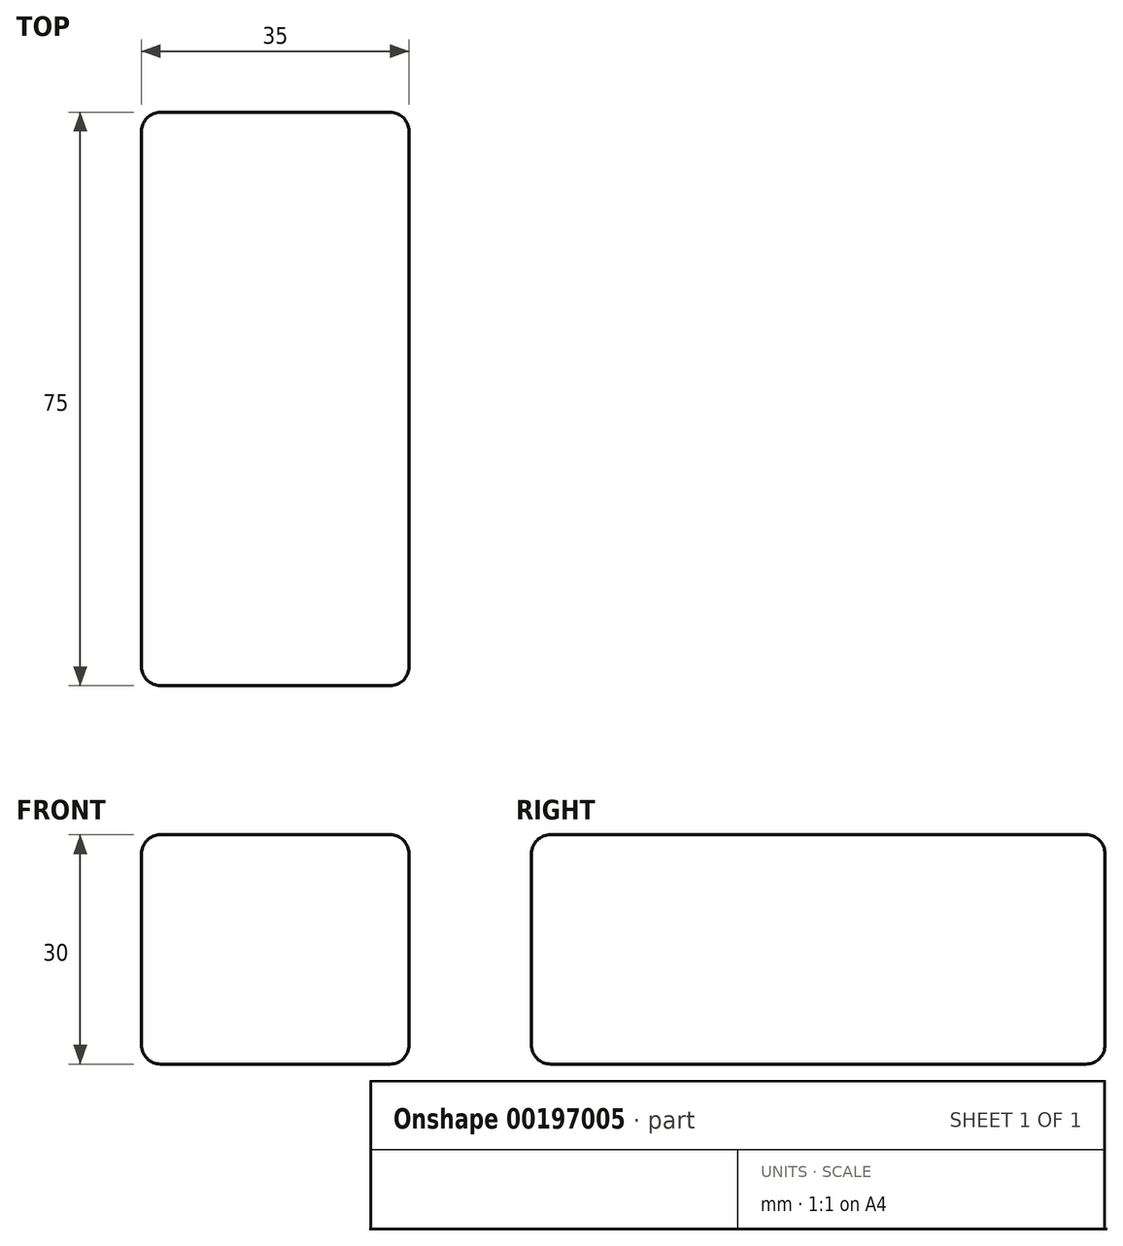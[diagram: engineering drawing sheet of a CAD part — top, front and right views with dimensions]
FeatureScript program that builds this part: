
annotation { "Feature Type Name" : "Feature", "Feature Type Description" : "" }
export const myFeature = defineFeature(function(context is Context, id is Id, definition is map)
    precondition{}
    {
        {
            var Q0;
            Q0=qCreatedBy(makeId("Top.planeOp"),FACE);
            var sketch = newSketch(context, id + "F0", { "sketchPlane" : qUnion([Q0])});
            skLineSegment(sketch, "E0.bottom", {"start": v(17.5, 37.5) * mm, "end": v(-17.5, 37.5) * mm});
            skLineSegment(sketch, "E0.top", {"start": v(17.5, -37.5) * mm, "end": v(-17.5, -37.5) * mm});
            skLineSegment(sketch, "E0.left", {"start": v(17.5, 37.5) * mm, "end": v(17.5, -37.5) * mm});
            skLineSegment(sketch, "E0.right", {"start": v(-17.5, 37.5) * mm, "end": v(-17.5, -37.5) * mm});
            skPoint(sketch, "E0.middle", {"position": v(0, 0) * mm});
            skSolve(sketch);
        }
        {
            var Q0;
            Q0 = qSketchRegion(id + "F0", true);
            extrude(context, id + "F1", {"entities" : qUnion([Q0]), "depth" : 30 * mm});
        }
        {
            var Q0;
            Q0=makeQuery(id+"F1.opExtrude","CAP_EDGE",EDGE,{"disambiguationData":[OSD([sQuery(id+"F0.wireOp",EDGE,"E0.bottom")])],"isStart":false});
            var Q1;
            Q1=makeQuery(id+"F1.opExtrude","CAP_EDGE",EDGE,{"disambiguationData":[OSD([sQuery(id+"F0.wireOp",EDGE,"E0.right")])],"isStart":false});
            var Q2;
            Q2=makeQuery(id+"F1.opExtrude","CAP_EDGE",EDGE,{"disambiguationData":[OSD([sQuery(id+"F0.wireOp",EDGE,"E0.top")])],"isStart":false});
            var Q3;
            Q3=makeQuery(id+"F1.opExtrude","CAP_EDGE",EDGE,{"disambiguationData":[OSD([sQuery(id+"F0.wireOp",EDGE,"E0.left")])],"isStart":false});
            var Q4;
            Q4=makeQuery(id+"F1.opExtrude","SWEPT_EDGE",EDGE,{"disambiguationData":[OSD([sQuery(id+"F0.wireOp",EDGE,"E0.top"),sQuery(id+"F0.wireOp",EDGE,"E0.left")])]});
            var Q5;
            Q5=makeQuery(id+"F1.opExtrude","SWEPT_EDGE",EDGE,{"disambiguationData":[OSD([sQuery(id+"F0.wireOp",EDGE,"E0.top"),sQuery(id+"F0.wireOp",EDGE,"E0.right")])]});
            var Q6;
            Q6=makeQuery(id+"F1.opExtrude","CAP_EDGE",EDGE,{"disambiguationData":[OSD([sQuery(id+"F0.wireOp",EDGE,"E0.top")])],"isStart":true});
            var Q7;
            Q7=makeQuery(id+"F1.opExtrude","CAP_EDGE",EDGE,{"disambiguationData":[OSD([sQuery(id+"F0.wireOp",EDGE,"E0.left")])],"isStart":true});
            var Q8;
            Q8=makeQuery(id+"F1.opExtrude","SWEPT_EDGE",EDGE,{"disambiguationData":[OSD([sQuery(id+"F0.wireOp",EDGE,"E0.bottom"),sQuery(id+"F0.wireOp",EDGE,"E0.left")])]});
            var Q9;
            Q9=makeQuery(id+"F1.opExtrude","CAP_EDGE",EDGE,{"disambiguationData":[OSD([sQuery(id+"F0.wireOp",EDGE,"E0.bottom")])],"isStart":true});
            var Q10;
            Q10=makeQuery(id+"F1.opExtrude","CAP_EDGE",EDGE,{"disambiguationData":[OSD([sQuery(id+"F0.wireOp",EDGE,"E0.right")])],"isStart":true});
            var Q11;
            Q11=makeQuery(id+"F1.opExtrude","SWEPT_EDGE",EDGE,{"disambiguationData":[OSD([sQuery(id+"F0.wireOp",EDGE,"E0.bottom"),sQuery(id+"F0.wireOp",EDGE,"E0.right")])]});
            fillet(context, id + "F2", {"entities" : qUnion([Q0, Q1, Q2, Q3, Q4, Q5, Q6, Q7, Q8, Q9, Q10, Q11]), "radius" : 2.5 * mm, "tangentPropagation" : true, "allowEdgeOverflow" : false});
        }
    });
